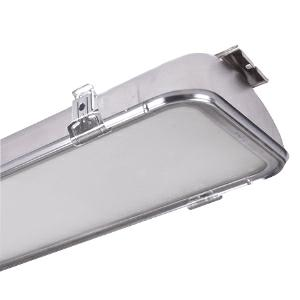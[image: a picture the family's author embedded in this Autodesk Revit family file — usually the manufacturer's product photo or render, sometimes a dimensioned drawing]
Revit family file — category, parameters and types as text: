
# Revit family: 3f_filippi_-_beta_235_93_vs_ampio_3f_filippi_-_52839_-_beta_235_led_932x50_dali_ampio_vs_l1565
name_source: partatom
category: Lighting Fixtures
units: mm (PartAtom-declared; Revit-internal decimal feet)

## family parameters
Cut with Voids When Loaded = No
Host = Face
Light Source = No
Part Type = Normal
Room Calculation Point = No
Round Connector Dimension = Use Diameter
Shared = No

## types (1)
- 3F Filippi - Beta 235 93 VS Ampio (1 x LED, 13793 lm, 99 W, 4000 K)
    Apparent Load = 99 VA
    Approval mark = CE
    CIE Flux Codes = 65 90 98 100 100
    Color Rendering = 80
    Color Temperature = 4000 K
    Control Gear = Electronic transformer
    Default Elevation = 1800 mm
    Description = ILLUMINOTECHNICAL
Luminous efficiency 100% (DLOR 100%, ULOR 0%).
Initial luminous flux of the luminaire 13793 lm.
Wide symmetric distribution.
Installation Interdistance Transv.D = 1.26 x hu - Long.D = 1.32 x hu.
Tabular UGR (CIE 117 - 4H-8H; S=0.25H; 70/50/20): RUG 21.3 - 22.4.
Beam angle: 87° - 92°.
Luminous efficacy 139 lm/W.
Lifetime (L93/B10): 30000 h. (tq+25°C)
Lifetime (L90/B10): 50000 h. (tq+25°C)
Lifetime (L85/B10): 80000 h. (tq+25°C)
Lifetime (L80/B10): 100000 h. (tq+25°C)
Lifetime (L85/B10): 50000 h. (tq+45°C)
Sudden decreased luminous flux after 50000 hours: 0% (C0).
Photobiological safety in compliance with IEC/TR 62778: RG0 risk exempt, (IEC 62471).
In compliance with IEC/EN 62722-2-1 - IEC/EN 62717 standards.

SOURCE
2 linear LED modules 50W/840.
Energy efficiency class (UE 2019/2020 - UE 2019/2015): C.
CIE 13.3 Colour rendering index: CRI >80 (R9 <50%).
IES TM-30 Fidelity Index: Rf = 84 Rg = 95.
CCT nominal colour temperature 4000 K.
Colour initial tolerance (MacAdam): SDCM 3.

MECHANICAL
Housing in AISI 304 stainless steel, pressed in one single piece.
VS moulded anti-glare glass, non-combustible, single-piece perimeter frame in stainless steel.
Oversized gear-tray reflector unit in highly reflective white painted hot-galvanised steel.
Methacrylate (PMMA) lenses with external flat surface.
Stainless steel snap-lock clips for diffuser mounting (safety n° 4 per fixture).
Luminaire with limited surface temperature. - D - (EN 60598-2-24)
Dimensions: 1565x235 mm, height 105 mm. Weight 11.31 kg.
IP65 protection degree.
Mechanical strength to impacts IK09 (10 joule).
Glow-wire test resistance 960°C.

ELECTRICAL
Halogen Free DALI-2 DATI (Parts 251, 252, 253), PUSH-DIM, electronic wiring 230V-50/60Hz, power factor 0.95 at full load, THD <25%, constant output current, class I, 1 driver, 1 DALI addresse.
Power of the luminaire 99 W.
ENEC - CE.
Flicker: <4%.
Luminaire compliant with EN 60598-2-22 for power supply from a centralised emergency system CPSS (Central Power Supply System), not incorporated in the luminaire - high risk areas excluded. The default power and flux are 100% in AC and 15% in DC.
Ambient temperature from -20°C to +45°C.
Temperature class T6 max 85°C.
Quick connection via M25 5P connector with 9-13 mm tightening range.
Relative humidity UR: <85%.

INSTALLATION
Ceiling / Suspended / Wall.
All accessories dedicated to this product are available on the Catalog and on our website www.3F-Filippi.com.

APPLICATIONS
Dry, dusty indoor environments, subject to occasional water splashes.
Any environments except the ones where the luminaire materials are unsuitable.
Industrial environments, warehouses, environments where security locks are required on all clips, e.g. prisons (on request).
Environments in which it is necessary a total protection against falling fragments (eg environments with foodstuffs or machines with moving parts or with extreme temperature changes), use luminaires with laminated glass.
Tempered glass is not immune to falling fragments from harmless and caused by shocks or exceptionally derived from the tempering process.

LIGHT MANAGEMENT
Recommended minimum setting: 10%.
The luminaire, equipped with (DALI-2 DATI) driver, can be controlled manually with 3F Easy Dim technology or automatically/manually with wired or wireless DALI/D2D control systems.
The D2D driver guarantees interoperability with other devices with the same certification by making the following information available:
Device Data (Part 251), Energy Report (Part 252), Diagnosis & Maintenance (Part 253).
In electrical systems without a regulation system (manual or automatic) and DALI bus, a suitable jumper must be made on the DA-DA terminals of the appliance.

WARNING
Fixture not suitable for cold stores with an ambient temperature <0°C and/or relative humidity >85%.
Luminaire designed for disposal/recycling at end-of-life.
Replaceable (LED only) light source by a professional. Replaceable control gear by a professional.
    Height = 105 mm
    Lamp = 1 x LED
    Lamp Light Flux = 13793 lm
    Lamp Power = 99 W
    Lamp count = 1
    Length = 1565 mm
    Lifetime = 50000 h
    Luminous efficacy = 139 lm/W
    Manufacturer = 3F Filippi
    ModVariant = No
    Model = 3F Filippi - 52839 - Beta 235 LED 932x50 DALI AMPIO VS L1565
    Mounting Place = Ceiling
    Mounting Type = Pendant
    Number of Poles = 1
    OnlyDefault = Yes
    Power Factor = 1
    Product Name = 3F Filippi - Beta 235 93 VS Ampio
    Product group = pendant luminaire
    ProductGroupID = 9
    Protection Class = Protection class I
    Protection Degree = IP 65
    RLX_Detail_Level = 1
    RLX_Emergency_Light_Flux = 0 lm
    RLX_Emergency_Type = 0
    RLX_Emergency_Type_DB = No
    RlxData = <blob elided: 84837 chars, md5=e67fd7e6>
    Socket = socket
    Standby Power = 0 W
    System Light Flux = 13793 lm
    System Power = 99 W
    Type Comments = Product without accessories
    Type Image = 3ffilippi_52839.jpg
    URL = http://relux.com
    VarID = ---
    Voltage = 0 V
    Weight = 0.00 kg
    Width = 235 mm

## geometry (parser evidence)
native form markers: Blend x4, Sweep x10
no freeform markers — native parametric forms only
